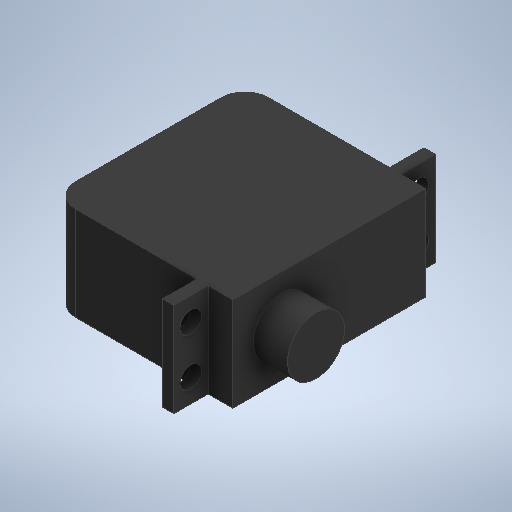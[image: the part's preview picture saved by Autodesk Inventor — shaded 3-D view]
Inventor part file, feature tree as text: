
AUTODESK INVENTOR PART (.ipt)
format: ipt  version: 2025 (Build 290162000, 162)  size: 284,160 bytes
history: native  units: mm
features: extrude x5, sketch x5, fillet x1
ambient origin geometry x8: Origin, YZ Plane, XZ Plane, XY Plane, X Axis, Y Axis, Z Axis, Center Point
bodies: Solide1 (feature_tree)
feature tree (11):
  extrude  "Extrusion1"  Depth=19.7mm
  extrude  "Extrusion2"  Depth=40.5mm
  extrude  "Extrusion3"  Depth=38.0mm TaperAngle=0.0deg
  extrude  "Extrusion4"  Depth=5.2mm
  extrude  "Extrusion5"  Depth=2.4mm
  fillet  "Congé1"  Radius=7.2mm
  sketch  "Esquisse1"
  sketch  "Esquisse2"
  sketch  "Esquisse3"
  sketch  "Esquisse4"
  sketch  "Esquisse5"
